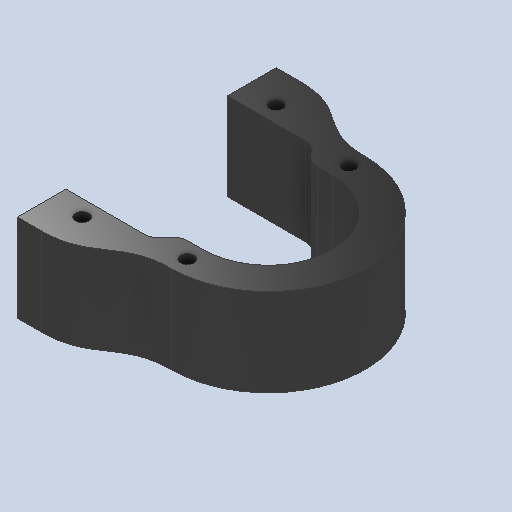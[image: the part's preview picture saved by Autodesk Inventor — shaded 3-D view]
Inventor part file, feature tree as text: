
AUTODESK INVENTOR PART (.ipt)
format: ipt  version: 2025.1 (Build 291241020, 241B)  size: 230,400 bytes
history: native  units: in
note: dims shown in document units (in); Inventor stores cm internally (conversion verified against a paired STEP export)
features: extrude x3, sketch x3
ambient origin geometry x8: Origin, YZ Plane, XZ Plane, XY Plane, X Axis, Y Axis, Z Axis, Center Point
bodies: Solid1 (feature_tree)
feature tree (6):
  extrude  "Extrusion1"  Depth=1.355in TaperAngle=0.0deg
  extrude  "Extrusion2"  Depth=1.06in TaperAngle=0.0deg
  extrude  "Extrusion3"  Depth=0.75in TaperAngle=0.0deg
  sketch  "Sketch1"  dims[d0=1.25in d1=1.355in d2=0.0in]
  sketch  "Sketch2"  dims[d3=0.5in d4=1.06in d5=0.0in]
  sketch  "Sketch3"  dims[d9=0.75in d10=0.5in d11=3.0in d12=4.0in d13=0.25in d14=0.75in d15=0.75in d16=0.75in d17=0.5in d18=3.0in d19=4.0in d20=0.25in d21=0.75in d22=0.75in d23=0.75in d24=0.5in d25=3.0in d26=4.0in d27=0.25in d28=0.75in d29=0.75in d30=0.75in d31=0.5in d32=3.0in d33=4.0in d34=0.25in d35=0.75in d36=0.75in d37=1.06in d38=0.0in]
